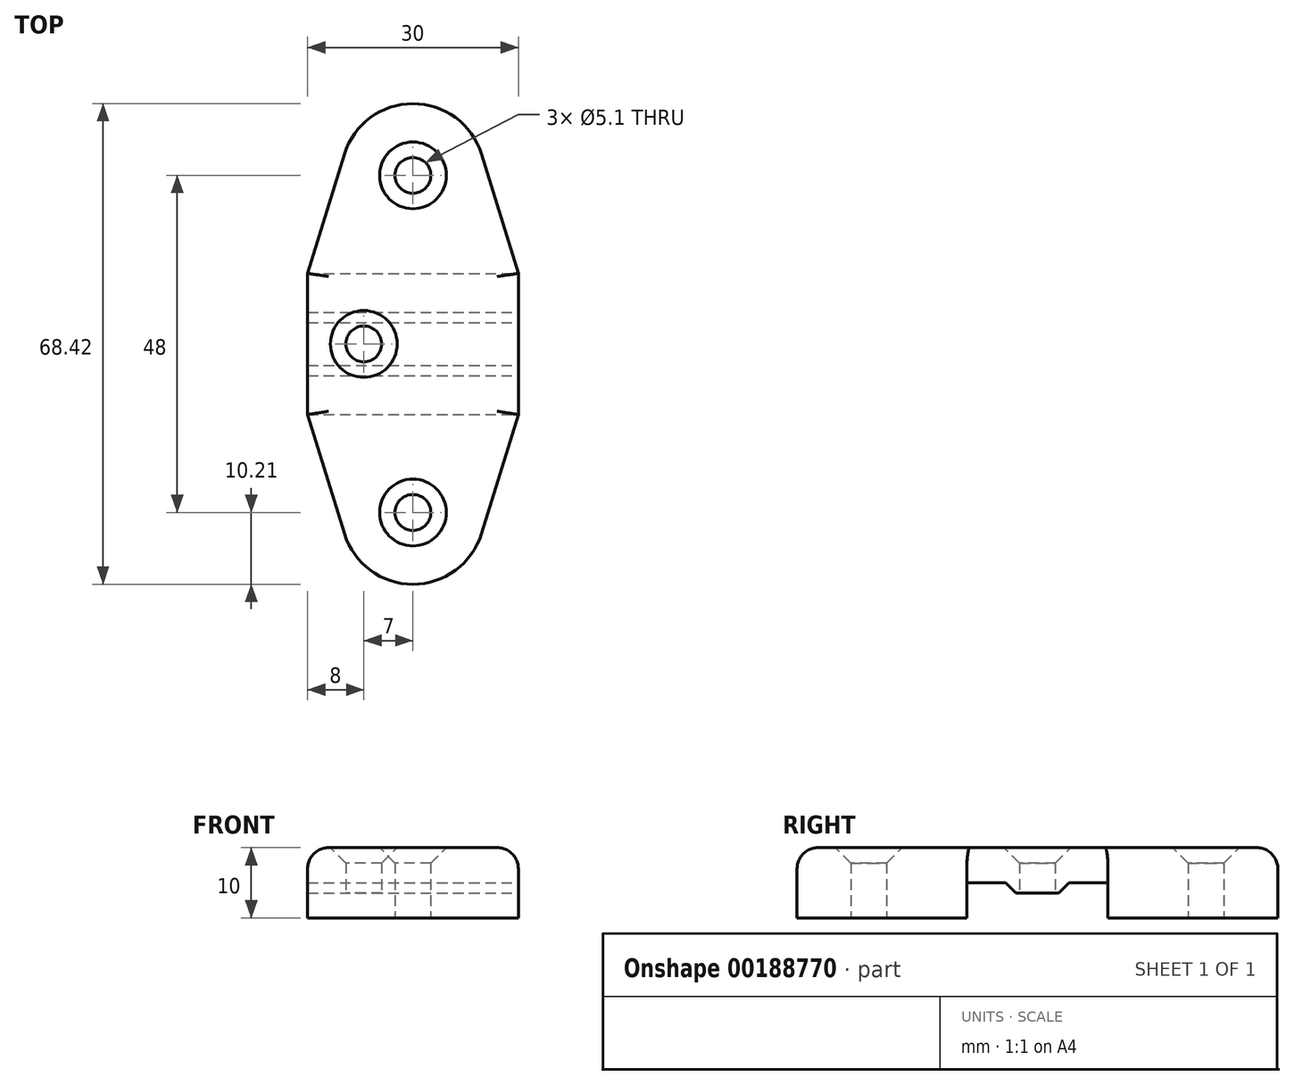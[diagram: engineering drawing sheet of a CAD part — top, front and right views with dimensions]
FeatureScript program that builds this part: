
annotation { "Feature Type Name" : "Feature", "Feature Type Description" : "" }
export const myFeature = defineFeature(function(context is Context, id is Id, definition is map)
    precondition{}
    {
        {
            var Q0;
            Q0=qCreatedBy(makeId("Top.planeOp"),FACE);
            var sketch = newSketch(context, id + "F0", { "sketchPlane" : qUnion([Q0])});
            skPoint(sketch, "E0.middle", {"position": v(0, 0) * mm});
            skCircle(sketch, "E1", {"center": v(0, -443415.28) * mm, "radius": 2.55 * mm});
            skCircle(sketch, "E2", {"center": v(0, -443463.28) * mm, "radius": 2.55 * mm});
            skLineSegment(sketch, "E3", {"start": v(-15, 10.05) * mm, "end": v(15, 10.05) * mm, "construction": true});
            skLineSegment(sketch, "E4", {"start": v(-15, -10.05) * mm, "end": v(15, -10.05) * mm, "construction": true});
            skLineSegment(sketch, "E5", {"start": v(-15, 10.05) * mm, "end": v(-9.76, 27.01) * mm});
            skLineSegment(sketch, "E6", {"start": v(15, 10.05) * mm, "end": v(9.76, 27.01) * mm});
            skLineSegment(sketch, "E7", {"start": v(-15, -10.05) * mm, "end": v(-9.76, -27.01) * mm});
            skLineSegment(sketch, "E8", {"start": v(15, -10.05) * mm, "end": v(9.76, -27.01) * mm});
            skLineSegment(sketch, "E9", {"start": v(0, 24) * mm, "end": v(0, -24) * mm, "construction": true});
            skCircle(sketch, "E10", {"center": v(-7, 0) * mm, "radius": 2.55 * mm});
            skLineSegment(sketch, "E11", {"start": v(-15, 10.05) * mm, "end": v(-15, -10.05) * mm});
            skLineSegment(sketch, "E12", {"start": v(15, 10.05) * mm, "end": v(15, -10.05) * mm});
            skLineSegment(sketch, "E13", {"start": v(-15, 0) * mm, "end": v(15, 0) * mm, "construction": true});
            skPoint(sketch, "E14", {"position": v(0, 10.05) * mm});
            skCircle(sketch, "E15", {"center": v(0, 24) * mm, "radius": 2.55 * mm});
            skCircle(sketch, "E16", {"center": v(0, -24) * mm, "radius": 2.55 * mm});
            skArc(sketch, "E17", {"start": v(-9.76, 27.01) * mm, "mid": v(0, 34.21) * mm, "end": v(9.76, 27.01) * mm});
            skArc(sketch, "E18", {"start": v(-9.76, -27.01) * mm, "mid": v(0, -34.21) * mm, "end": v(9.76, -27.01) * mm});
            skSolve(sketch);
        }
        {
            var Q0;
            Q0=makeQuery(id+"F0.imprint","IMPRINT",FACE,{"disambiguationData":[TD([[makeQuery(id+"F0.imprint","IMPRINT",EDGE,{"derivedFrom":sQuery(id+"F0.wireOp",EDGE,"E5")}),-1.0]])]});
            extrude(context, id + "F1", {"entities" : qUnion([Q0]), "depth" : 10 * mm, "offsetDistance" : 25 * mm});
        }
        {
            var Q0;
            Q0=makeQuery(id+"F1.opExtrude","SWEPT_FACE",FACE,{"disambiguationData":[OSD([sQuery(id+"F0.wireOp",EDGE,"E12")])]});
            var sketch = newSketch(context, id + "F2", { "sketchPlane" : qUnion([Q0])});
            skLineSegment(sketch, "E19", {"start": v(0, 0) * mm, "end": v(0, 10) * mm, "construction": true});
            skLineSegment(sketch, "E20.bottom", {"start": v(-10.05, 0) * mm, "end": v(10.05, 0) * mm});
            skLineSegment(sketch, "E20.top", {"start": v(-10.05, 5) * mm, "end": v(10.05, 5) * mm});
            skLineSegment(sketch, "E20.left", {"start": v(-10.05, 0) * mm, "end": v(-10.05, 5) * mm});
            skLineSegment(sketch, "E20.right", {"start": v(10.05, 0) * mm, "end": v(10.05, 5) * mm});
            skSolve(sketch);
        }
        {
            var Q0;
            Q0=makeQuery(id+"F2.imprint","IMPRINT",FACE,{"disambiguationData":[TD([[makeQuery(id+"F2.imprint","IMPRINT",EDGE,{"derivedFrom":sQuery(id+"F2.wireOp",EDGE,"E20.bottom")}),-1.0]])]});
            extrude(context, id + "F3", {"entities" : qUnion([Q0]), "operationType" : NewBodyOperationType.REMOVE, "endBound" : BoundingType.THROUGH_ALL, "oppositeDirection" : true, "depth" : 25 * mm, "offsetDistance" : 25 * mm});
        }
        {
            var Q0;
            Q0=makeQuery(id+"F1.opExtrude","SWEPT_FACE",FACE,{"disambiguationData":[OSD([sQuery(id+"F0.wireOp",EDGE,"E12")])]});
            var sketch = newSketch(context, id + "F4", { "sketchPlane" : qUnion([Q0])});
            skLineSegment(sketch, "E21", {"start": v(4.5, 5) * mm, "end": v(3.05, 3.54) * mm});
            skLineSegment(sketch, "E22", {"start": v(3.05, 3.55) * mm, "end": v(-3.05, 3.54) * mm});
            skLineSegment(sketch, "E23", {"start": v(-3.05, 3.55) * mm, "end": v(-4.5, 5) * mm});
            skLineSegment(sketch, "E24", {"start": v(0, 10) * mm, "end": v(0, 5) * mm, "construction": true});
            skSolve(sketch);
        }
        {
            var Q0;
            {var subQ0=sQuery(id+"F4.wireOp",EDGE,"E21");Q0=makeQuery(id+"F4.imprint","IMPRINT",FACE,{"disambiguationData":[TD([[makeQuery(id+"F4.imprint","IMPRINT",EDGE,{"derivedFrom":subQ0}),-1.0]])]});}
            var Q1;
            Q1=makeQuery(id+"F1.opExtrude","SWEPT_FACE",FACE,{"disambiguationData":[OSD([sQuery(id+"F0.wireOp",EDGE,"E11")])]});
            extrude(context, id + "F5", {"entities" : qUnion([Q0]), "operationType" : NewBodyOperationType.ADD, "endBound" : BoundingType.UP_TO_SURFACE, "oppositeDirection" : true, "depth" : 25 * mm, "endBoundEntityFace" : qUnion([Q1]), "offsetDistance" : 25 * mm});
        }
        {
            var Q0;
            Q0=makeQuery(id+"F0.imprint","IMPRINT",FACE,{"disambiguationData":[TD([[makeQuery(id+"F0.imprint","IMPRINT",EDGE,{"derivedFrom":sQuery(id+"F0.wireOp",EDGE,"E10")}),1.0]])]});
            var Q1;
            Q1=makeQuery(id+"F1.opExtrude","CAP_FACE",FACE,{"disambiguationData":[OSD([sQuery(id+"F0.wireOp",EDGE,"E0.left"),sQuery(id+"F0.wireOp",EDGE,"E0.right"),sQuery(id+"F0.wireOp",EDGE,"E1"),sQuery(id+"F0.wireOp",EDGE,"E2"),sQuery(id+"F0.wireOp",EDGE,"E5"),sQuery(id+"F0.wireOp",EDGE,"E6"),sQuery(id+"F0.wireOp",EDGE,"E7"),sQuery(id+"F0.wireOp",EDGE,"E8"),sQuery(id+"F0.wireOp",EDGE,"SBfZ0ZaC-sz1m-Xk8u-0noZ-aNedcS73Bl8m"),sQuery(id+"F0.wireOp",EDGE,"lhAWZnUN-VowD-uL3P-NqKj-8G4JGcrHoMbx")])],"isStart":false});
            extrude(context, id + "F6", {"entities" : qUnion([Q0]), "operationType" : NewBodyOperationType.REMOVE, "endBound" : BoundingType.UP_TO_SURFACE, "depth" : 25 * mm, "endBoundEntityFace" : qUnion([Q1]), "offsetDistance" : 25 * mm});
        }
        {
            var Q0;
            Q0=makeQuery(id+"F1.opExtrude","CAP_EDGE",EDGE,{"disambiguationData":[OSD([sQuery(id+"F0.wireOp",EDGE,"E5")])],"isStart":false});
            var Q1;
            Q1=makeQuery(id+"F1.opExtrude","CAP_EDGE",EDGE,{"disambiguationData":[OSD([sQuery(id+"F0.wireOp",EDGE,"SBfZ0ZaC-sz1m-Xk8u-0noZ-aNedcS73Bl8m")])],"isStart":false});
            var Q2;
            Q2=makeQuery(id+"F1.opExtrude","CAP_EDGE",EDGE,{"disambiguationData":[OSD([sQuery(id+"F0.wireOp",EDGE,"E6")])],"isStart":false});
            var Q3;
            Q3=makeQuery(id+"F1.opExtrude","CAP_EDGE",EDGE,{"disambiguationData":[OSD([sQuery(id+"F0.wireOp",EDGE,"E0.left")])],"isStart":false});
            var Q4;
            Q4=makeQuery(id+"F1.opExtrude","CAP_EDGE",EDGE,{"disambiguationData":[OSD([sQuery(id+"F0.wireOp",EDGE,"E8")])],"isStart":false});
            var Q5;
            Q5=makeQuery(id+"F1.opExtrude","CAP_EDGE",EDGE,{"disambiguationData":[OSD([sQuery(id+"F0.wireOp",EDGE,"lhAWZnUN-VowD-uL3P-NqKj-8G4JGcrHoMbx")])],"isStart":false});
            var Q6;
            Q6=makeQuery(id+"F1.opExtrude","CAP_EDGE",EDGE,{"disambiguationData":[OSD([sQuery(id+"F0.wireOp",EDGE,"E7")])],"isStart":false});
            var Q7;
            Q7=makeQuery(id+"F1.opExtrude","CAP_EDGE",EDGE,{"disambiguationData":[OSD([sQuery(id+"F0.wireOp",EDGE,"E0.right")])],"isStart":false});
            var Q8;
            Q8=makeQuery(id+"F1.opExtrude","CAP_EDGE",EDGE,{"disambiguationData":[OSD([sQuery(id+"F0.wireOp",EDGE,"E12")])],"isStart":false});
            var Q9;
            Q9=makeQuery(id+"F1.opExtrude","CAP_EDGE",EDGE,{"disambiguationData":[OSD([sQuery(id+"F0.wireOp",EDGE,"E11")])],"isStart":false});
            fillet(context, id + "F7", {"entities" : qUnion([Q0, Q1, Q2, Q3, Q4, Q5, Q6, Q7, Q8, Q9]), "radius" : 3 * mm, "tangentPropagation" : true, "allowEdgeOverflow" : false});
        }
        {
            var Q0;
            Q0=makeQuery(id+"F1.opExtrude","CAP_EDGE",EDGE,{"disambiguationData":[OSD([sQuery(id+"F0.wireOp",EDGE,"E16")])],"isStart":false});
            var Q1;
            Q1=makeQuery(id+"F1.opExtrude","CAP_EDGE",EDGE,{"disambiguationData":[OSD([sQuery(id+"F0.wireOp",EDGE,"E10")])],"isStart":false});
            var Q2;
            Q2=makeQuery(id+"F1.opExtrude","CAP_EDGE",EDGE,{"disambiguationData":[OSD([sQuery(id+"F0.wireOp",EDGE,"E15")])],"isStart":false});
            chamfer(context, id + "F8", {"entities" : qUnion([Q0, Q1, Q2]), "width" : 2.2 * mm, "tangentPropagation" : true});
        }
    });
